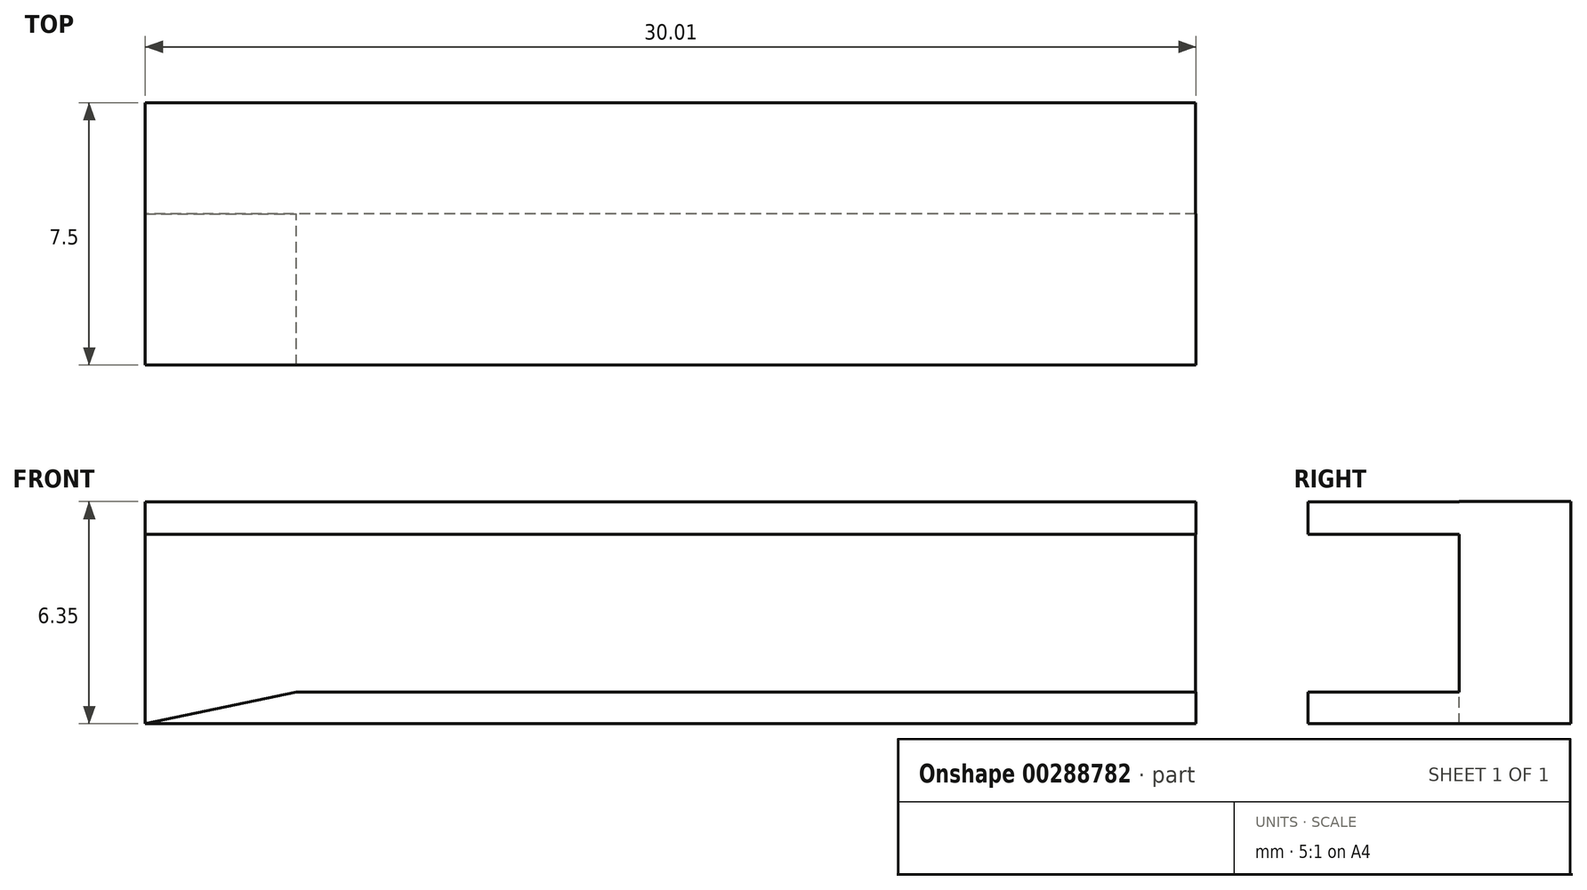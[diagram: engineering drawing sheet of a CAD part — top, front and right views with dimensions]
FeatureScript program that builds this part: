
annotation { "Feature Type Name" : "Feature", "Feature Type Description" : "" }
export const myFeature = defineFeature(function(context is Context, id is Id, definition is map)
    precondition{}
    {
        {
            var Q0;
            Q0=qCreatedBy(makeId("Front.planeOp"),FACE);
            var sketch = newSketch(context, id + "F0", { "sketchPlane" : qUnion([Q0])});
            skLineSegment(sketch, "E0.bottom", {"start": v(0, 0) * mm, "end": v(30, 0) * mm});
            skLineSegment(sketch, "E0.top", {"start": v(0, 6.35) * mm, "end": v(30, 6.35) * mm});
            skLineSegment(sketch, "E0.left", {"start": v(0, 0) * mm, "end": v(0, 6.35) * mm});
            skLineSegment(sketch, "E0.right", {"start": v(30, 0) * mm, "end": v(30, 6.35) * mm});
            skSolve(sketch);
        }
        {
            var Q0;
            Q0=makeQuery(id+"F0.imprint","IMPRINT",FACE,{"disambiguationData":[TD([[makeQuery(id+"F0.imprint","IMPRINT",EDGE,{"derivedFrom":sQuery(id+"F0.wireOp",EDGE,"E0.bottom")}),1.0]])]});
            extrude(context, id + "F1", {"entities" : qUnion([Q0]), "depth" : 3.18 * mm});
        }
        {
            var Q0;
            Q0=qCreatedBy(makeId("Front.planeOp"),FACE);
            var sketch = newSketch(context, id + "F2", { "sketchPlane" : qUnion([Q0])});
            skLineSegment(sketch, "E1", {"start": v(43.83, 9.27) * mm, "end": v(0, 0) * mm});
            skLineSegment(sketch, "E2", {"start": v(0, 0) * mm, "end": v(0, 6.32) * mm});
            skLineSegment(sketch, "E3", {"start": v(0, 6.32) * mm, "end": v(29.9, 0) * mm});
            skLineSegment(sketch, "E4.bottom", {"start": v(-0.05, 5.41) * mm, "end": v(29.95, 5.41) * mm});
            skLineSegment(sketch, "E4.top", {"start": v(-0.05, 0.91) * mm, "end": v(29.95, 0.91) * mm});
            skLineSegment(sketch, "E4.left", {"start": v(-0.05, 5.41) * mm, "end": v(-0.05, 0.91) * mm});
            skLineSegment(sketch, "E4.right", {"start": v(29.95, 5.41) * mm, "end": v(29.95, 0.91) * mm});
            skPoint(sketch, "E4.middle", {"position": v(14.95, 3.16) * mm});
            skLineSegment(sketch, "E5.bottom", {"start": v(30, 6.34) * mm, "end": v(0, 6.34) * mm});
            skLineSegment(sketch, "E5.top", {"start": v(30, 5.41) * mm, "end": v(0, 5.41) * mm});
            skLineSegment(sketch, "E5.left", {"start": v(30, 6.34) * mm, "end": v(30, 5.41) * mm});
            skLineSegment(sketch, "E5.right", {"start": v(0, 6.34) * mm, "end": v(0, 5.41) * mm});
            skLineSegment(sketch, "E6.bottom", {"start": v(0, 0) * mm, "end": v(30, 0) * mm});
            skLineSegment(sketch, "E6.top", {"start": v(0, 0.91) * mm, "end": v(30, 0.91) * mm});
            skLineSegment(sketch, "E6.left", {"start": v(0, 0) * mm, "end": v(0, 0.91) * mm});
            skLineSegment(sketch, "E6.right", {"start": v(30, 0) * mm, "end": v(30, 0.91) * mm});
            skSolve(sketch);
        }
        {
            var Q0;
            {var subQ7=sQuery(id+"F2.wireOp",EDGE,"E5.bottom");Q0=makeQuery(id+"F2.imprint","IMPRINT",FACE,{"disambiguationData":[TD([[makeQuery(id+"F2.imprint","IMPRINT",EDGE,{"derivedFrom":subQ7}),1.0]])]});}
            var Q1;
            {var subQ0=sQuery(id+"F2.wireOp",EDGE,"E5.right");var subQ1=sQuery(id+"F2.wireOp",EDGE,"E3");var subQ2=makeQuery(id+"F2.imprint","INTERSECT",VERTEX,{"derivedFrom":[subQ1,subQ0]});Q1=makeQuery(id+"F2.imprint","IMPRINT",FACE,{"disambiguationData":[TD([[makeQuery(id+"F2.imprint","IMPRINT",EDGE,{"disambiguationData":[TD([[subQ2,-1.0]])],"derivedFrom":subQ1}),-1.0]])]});}
            var Q2;
            {var subQ0=sQuery(id+"F2.wireOp",EDGE,"E5.left");Q2=makeQuery(id+"F2.imprint","IMPRINT",FACE,{"disambiguationData":[TD([[makeQuery(id+"F2.imprint","IMPRINT",EDGE,{"derivedFrom":subQ0}),-1.0]])]});}
            var Q3;
            {var subQ2=sQuery(id+"F2.wireOp",EDGE,"E6.right");Q3=makeQuery(id+"F2.imprint","IMPRINT",FACE,{"disambiguationData":[TD([[makeQuery(id+"F2.imprint","IMPRINT",EDGE,{"derivedFrom":subQ2}),1.0]])]});}
            var Q4;
            {var subQ0=sQuery(id+"F2.wireOp",EDGE,"E6.bottom");var subQ5=sQuery(id+"F2.wireOp",EDGE,"E3");var subQ6=makeQuery(id+"F2.imprint","INTERSECT",VERTEX,{"derivedFrom":[subQ5,subQ0]});Q4=makeQuery(id+"F2.imprint","IMPRINT",FACE,{"disambiguationData":[TD([[makeQuery(id+"F2.imprint","IMPRINT",EDGE,{"disambiguationData":[TD([[subQ6,1.0]])],"derivedFrom":subQ5}),-1.0]])]});}
            var Q5;
            {var subQ0=sQuery(id+"F2.wireOp",EDGE,"E6.left");Q5=makeQuery(id+"F2.imprint","IMPRINT",FACE,{"disambiguationData":[TD([[makeQuery(id+"F2.imprint","IMPRINT",EDGE,{"derivedFrom":subQ0}),-1.0]])]});}
            extrude(context, id + "F3", {"entities" : qUnion([Q0, Q1, Q2, Q3, Q4, Q5]), "operationType" : NewBodyOperationType.ADD, "depth" : 7.5 * mm});
        }
    });
